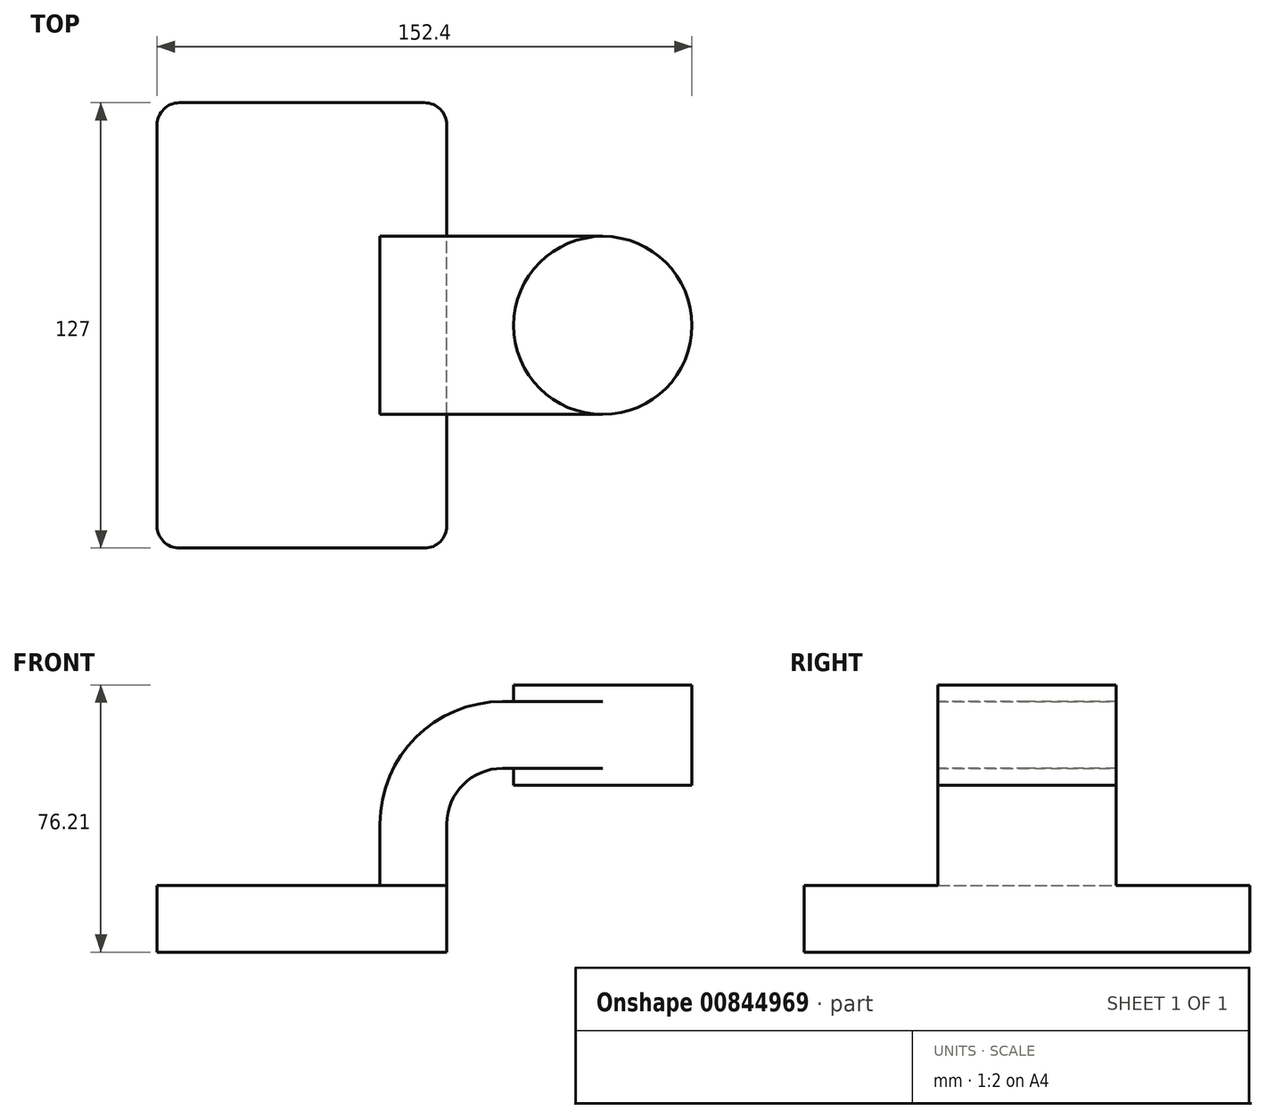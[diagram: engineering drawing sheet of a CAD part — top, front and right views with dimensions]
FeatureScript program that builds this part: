
annotation { "Feature Type Name" : "Feature", "Feature Type Description" : "" }
export const myFeature = defineFeature(function(context is Context, id is Id, definition is map)
    precondition{}
    {
        {
            var Q0;
            Q0=qCreatedBy(makeId("Front.planeOp"),FACE);
            var sketch = newSketch(context, id + "F0", { "sketchPlane" : qUnion([Q0])});
            skLineSegment(sketch, "E0.bottom", {"start": v(-41.27, -9.53) * mm, "end": v(41.28, -9.53) * mm});
            skLineSegment(sketch, "E0.top", {"start": v(-41.28, 9.53) * mm, "end": v(41.28, 9.53) * mm});
            skLineSegment(sketch, "E0.left", {"start": v(-41.28, -9.53) * mm, "end": v(-41.28, 9.53) * mm});
            skLineSegment(sketch, "E0.right", {"start": v(41.28, -9.53) * mm, "end": v(41.28, 9.53) * mm});
            skPoint(sketch, "E0.middle", {"position": v(0, 0) * mm});
            skLineSegment(sketch, "E1.bottom", {"start": v(60.32, 38.1) * mm, "end": v(111.12, 38.1) * mm});
            skLineSegment(sketch, "E1.top", {"start": v(60.32, 66.67) * mm, "end": v(111.12, 66.67) * mm});
            skLineSegment(sketch, "E1.left", {"start": v(60.32, 38.1) * mm, "end": v(60.32, 66.67) * mm});
            skLineSegment(sketch, "E1.right", {"start": v(111.12, 38.1) * mm, "end": v(111.12, 66.67) * mm});
            skPoint(sketch, "E1.middle", {"position": v(85.72, 52.39) * mm});
            skLineSegment(sketch, "E2", {"start": v(41.28, 9.52) * mm, "end": v(41.28, 27) * mm});
            skArc(sketch, "E3", {"start": v(41.27, 27) * mm, "mid": v(45.92, 38.23) * mm, "end": v(57.15, 42.88) * mm});
            skLineSegment(sketch, "E4", {"start": v(57.15, 42.88) * mm, "end": v(85.72, 42.88) * mm});
            skLineSegment(sketch, "E5.0", {"start": v(57.15, 61.93) * mm, "end": v(85.72, 61.93) * mm});
            skArc(sketch, "E5.1", {"start": v(22.23, 27) * mm, "mid": v(32.45, 51.7) * mm, "end": v(57.15, 61.93) * mm});
            skLineSegment(sketch, "E5.2", {"start": v(22.22, 9.52) * mm, "end": v(22.22, 27) * mm});
            skLineSegment(sketch, "E6", {"start": v(85.72, 38.1) * mm, "end": v(85.72, 66.67) * mm});
            skFitSpline(sketch, "E7", {"points": [v(-41.27, 9.53) * mm, v(57.15, 61.93) * mm], "startDerivative": vector(0.27, 111.5) * mm, "endDerivative": vector(134.44, -2.13) * mm});
            skSolve(sketch);
        }
        {
            var Q0;
            Q0=makeQuery(id+"F0.imprint","IMPRINT",FACE,{"disambiguationData":[TD([[makeQuery(id+"F0.imprint","IMPRINT",EDGE,{"derivedFrom":sQuery(id+"F0.wireOp",EDGE,"E0.bottom")}),1.0]])]});
            extrude(context, id + "F1", {"entities" : qUnion([Q0]), "endBound" : BoundingType.SYMMETRIC, "depth" : 127 * mm, "offsetDistance" : 25.4 * mm});
        }
        {
            var Q0;
            {var subQ1=sQuery(id+"F0.wireOp",EDGE,"E2");Q0=makeQuery(id+"F0.imprint","IMPRINT",FACE,{"disambiguationData":[TD([[makeQuery(id+"F0.imprint","IMPRINT",EDGE,{"derivedFrom":subQ1}),1.0]])]});}
            var Q1;
            {var subQ0=sQuery(id+"F0.wireOp",EDGE,"E4");var subQ1=sQuery(id+"F0.wireOp",EDGE,"E1.left");var subQ2=makeQuery(id+"F0.imprint","INTERSECT",VERTEX,{"derivedFrom":[subQ1,subQ0]});Q1=makeQuery(id+"F0.imprint","IMPRINT",FACE,{"disambiguationData":[TD([[makeQuery(id+"F0.imprint","IMPRINT",EDGE,{"disambiguationData":[TD([[subQ2,-1.0]])],"derivedFrom":subQ1}),-1.0]])]});}
            extrude(context, id + "F2", {"entities" : qUnion([Q0, Q1]), "operationType" : NewBodyOperationType.ADD, "endBound" : BoundingType.SYMMETRIC, "depth" : 50.8 * mm, "offsetDistance" : 25.4 * mm});
        }
        {
            var Q0;
            Q0=makeQuery(id+"F0.imprint","IMPRINT",FACE,{"disambiguationData":[TD([[makeQuery(id+"F0.imprint","IMPRINT",EDGE,{"derivedFrom":sQuery(id+"F0.wireOp",EDGE,"E5.1")}),1.0]])]});
            extrude(context, id + "F3", {"entities" : qUnion([Q0]), "operationType" : NewBodyOperationType.ADD, "endBound" : BoundingType.SYMMETRIC, "depth" : 15.88 * mm, "offsetDistance" : 25.4 * mm});
        }
        {
            var Q0;
            {var subQ0=sQuery(id+"F0.wireOp",EDGE,"E1.right");Q0=makeQuery(id+"F0.imprint","IMPRINT",FACE,{"disambiguationData":[TD([[makeQuery(id+"F0.imprint","IMPRINT",EDGE,{"derivedFrom":subQ0}),1.0]])]});}
            var Q1;
            Q1=sQuery(id+"F0.wireOp",EDGE,"E6");
            revolve(context, id + "F4", {"operationType" : NewBodyOperationType.ADD, "surfaceOperationType" : NewSurfaceOperationType.NEW, "entities" : qUnion([Q0]), "axis" : qUnion([Q1]), "revolveType" : RevolveType.FULL});
        }
        {
            var Q0;
            Q0=makeQuery(id+"F1.opExtrude","CAP_EDGE",EDGE,{"disambiguationData":[OSD([sQuery(id+"F0.wireOp",EDGE,"E0.right")])],"isStart":false});
            var Q1;
            Q1=makeQuery(id+"F1.opExtrude","CAP_EDGE",EDGE,{"disambiguationData":[OSD([sQuery(id+"F0.wireOp",EDGE,"E0.left")])],"isStart":false});
            var Q2;
            Q2=makeQuery(id+"F1.opExtrude","CAP_EDGE",EDGE,{"disambiguationData":[OSD([sQuery(id+"F0.wireOp",EDGE,"E0.left")])],"isStart":true});
            var Q3;
            Q3=makeQuery(id+"F1.opExtrude","CAP_EDGE",EDGE,{"disambiguationData":[OSD([sQuery(id+"F0.wireOp",EDGE,"E0.right")])],"isStart":true});
            fillet(context, id + "F5", {"entities" : qUnion([Q0, Q1, Q2, Q3]), "radius" : 6.35 * mm, "tangentPropagation" : true, "allowEdgeOverflow" : false});
        }
    });
